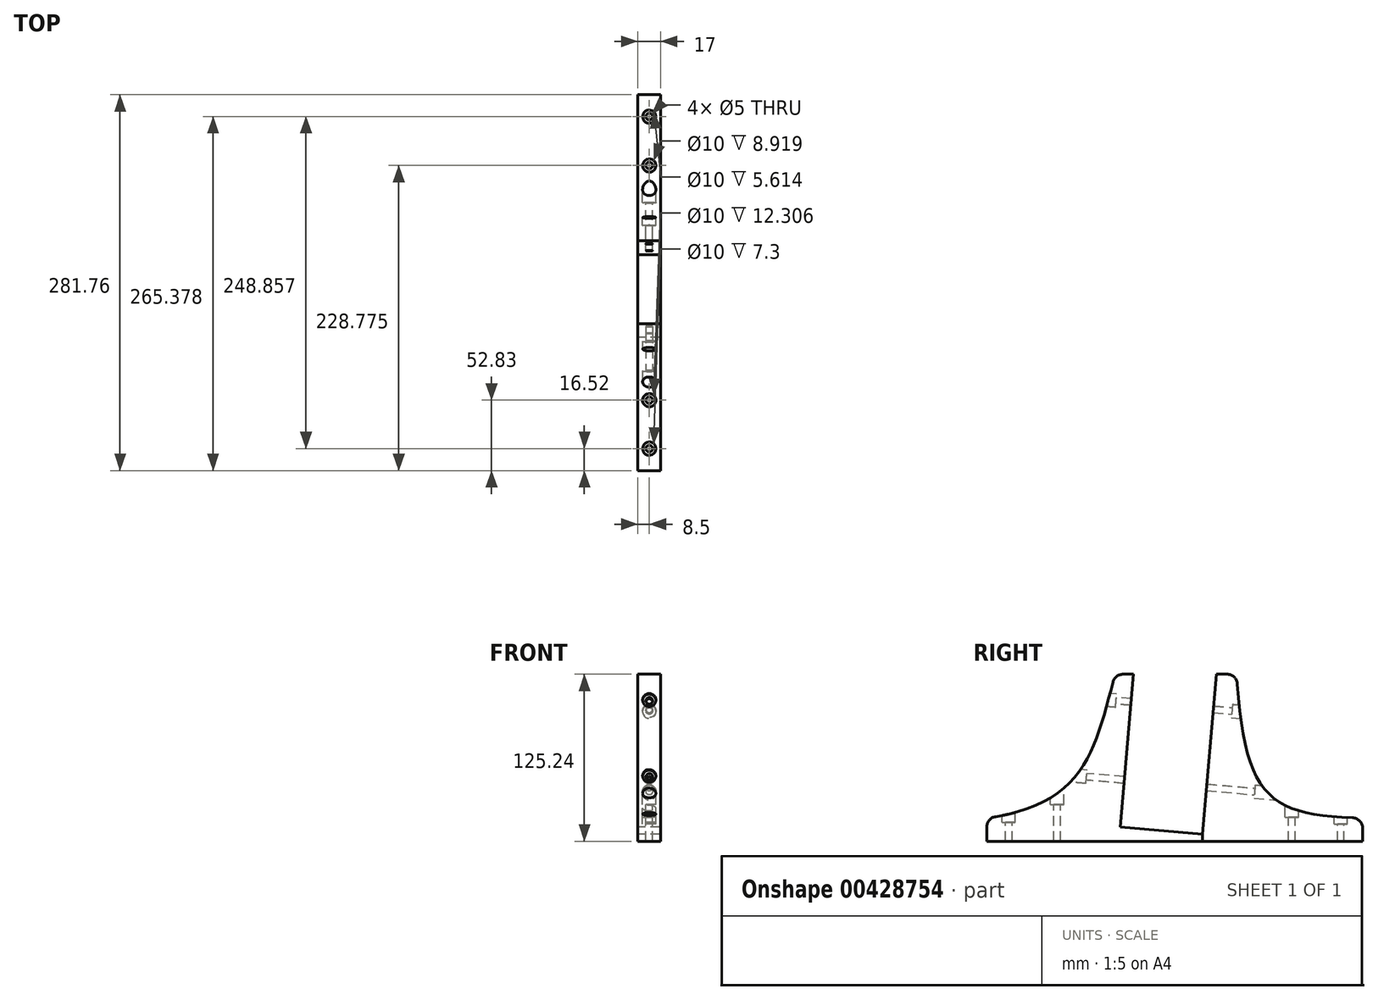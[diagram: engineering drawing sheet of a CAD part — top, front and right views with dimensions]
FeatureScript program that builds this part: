
annotation { "Feature Type Name" : "Feature", "Feature Type Description" : "" }
export const myFeature = defineFeature(function(context is Context, id is Id, definition is map)
    precondition{}
    {
        {
            var Q0;
            Q0=qCreatedBy(makeId("Right.planeOp"),FACE);
            var sketch = newSketch(context, id + "F0", { "sketchPlane" : qUnion([Q0])});
            skLineSegment(sketch, "E0.bottom", {"start": v(0, 0) * mm, "end": v(61.76, -5.4) * mm});
            skLineSegment(sketch, "E0.top", {"start": v(104.59, 1195.43) * mm, "end": v(166.35, 1190.03) * mm});
            skLineSegment(sketch, "E0.left", {"start": v(0, 0) * mm, "end": v(104.59, 1195.43) * mm});
            skLineSegment(sketch, "E0.right", {"start": v(61.76, -5.4) * mm, "end": v(166.35, 1190.03) * mm});
            skLineSegment(sketch, "E1", {"start": v(-100, -5.4) * mm, "end": v(-100, 6.83) * mm});
            skPoint(sketch, "E2.endSnap0", {"position": v(-29.12, -5.4) * mm});
            skLineSegment(sketch, "E3", {"start": v(-3.76, 114.6) * mm, "end": v(10.03, 114.6) * mm});
            skFitSpline(sketch, "E4", {"points": [v(-3.76, 114.6) * mm, v(-100, 6.83) * mm], "startDerivative": vector(-42.9, -159.15) * mm, "endDerivative": vector(-227.38, -28.7) * mm});
            skLineSegment(sketch, "E5", {"start": v(72.26, 114.6) * mm, "end": v(87.42, 114.6) * mm});
            skLineSegment(sketch, "E6", {"start": v(181.76, -5.4) * mm, "end": v(181.76, 6.83) * mm});
            skFitSpline(sketch, "E7", {"points": [v(87.42, 114.6) * mm, v(181.76, 6.83) * mm], "startDerivative": vector(16.8, -278.9) * mm, "endDerivative": vector(212.62, -4.06) * mm});
            skLineSegment(sketch, "E8", {"start": v(-100, -5.4) * mm, "end": v(-100, -10.64) * mm});
            skLineSegment(sketch, "E9", {"start": v(-100, -10.64) * mm, "end": v(181.76, -10.64) * mm});
            skLineSegment(sketch, "E10", {"start": v(181.76, -10.64) * mm, "end": v(181.76, -5.4) * mm});
            skLineSegment(sketch, "E11", {"start": v(61.76, -5.4) * mm, "end": v(61.76, -10.64) * mm});
            skSolve(sketch);
        }
        {
            var Q0;
            {var subQ1=sQuery(id+"F0.wireOp",EDGE,"E0.bottom");Q0=makeQuery(id+"F0.imprint","IMPRINT",FACE,{"disambiguationData":[TD([[makeQuery(id+"F0.imprint","IMPRINT",EDGE,{"derivedFrom":subQ1}),-1.0]])]});}
            extrude(context, id + "F1", {"entities" : qUnion([Q0]), "depth" : 17 * mm});
        }
        {
            var Q0;
            {var subQ0=sQuery(id+"F0.wireOp",EDGE,"E5");Q0=makeQuery(id+"F0.imprint","IMPRINT",FACE,{"disambiguationData":[TD([[makeQuery(id+"F0.imprint","IMPRINT",EDGE,{"derivedFrom":subQ0}),-1.0]])]});}
            extrude(context, id + "F2", {"entities" : qUnion([Q0]), "depth" : 17 * mm});
        }
        {
            var Q0;
            Q0=makeQuery(id+"F1.opExtrude","SWEPT_EDGE",EDGE,{"disambiguationData":[OSD([sQuery(id+"F0.wireOp",EDGE,"E1"),sQuery(id+"F0.wireOp",EDGE,"E4")])]});
            var Q1;
            Q1=makeQuery(id+"F1.opExtrude","SWEPT_EDGE",EDGE,{"disambiguationData":[OSD([sQuery(id+"F0.wireOp",EDGE,"E3"),sQuery(id+"F0.wireOp",EDGE,"E4")])]});
            var Q2;
            Q2=makeQuery(id+"F1.opExtrude","SWEPT_EDGE",EDGE,{"disambiguationData":[OSD([sQuery(id+"F0.wireOp",EDGE,"E6"),sQuery(id+"F0.wireOp",EDGE,"E7")])]});
            var Q3;
            Q3=makeQuery(id+"F1.opExtrude","SWEPT_EDGE",EDGE,{"disambiguationData":[OSD([sQuery(id+"F0.wireOp",EDGE,"E5"),sQuery(id+"F0.wireOp",EDGE,"E7")])]});
            var Q4;
            Q4=makeQuery(id+"F2.opExtrude","SWEPT_EDGE",EDGE,{"disambiguationData":[OSD([sQuery(id+"F0.wireOp",EDGE,"E5"),sQuery(id+"F0.wireOp",EDGE,"E7")])]});
            var Q5;
            Q5=makeQuery(id+"F2.opExtrude","SWEPT_EDGE",EDGE,{"disambiguationData":[OSD([sQuery(id+"F0.wireOp",EDGE,"E6"),sQuery(id+"F0.wireOp",EDGE,"E7")])]});
            fillet(context, id + "F3", {"entities" : qUnion([Q0, Q1, Q2, Q3, Q4, Q5]), "radius" : 8 * mm, "tangentPropagation" : true, "allowEdgeOverflow" : false});
        }
        {
            var Q0;
            Q0=makeQuery(id+"F1.opExtrude","SWEPT_FACE",FACE,{"disambiguationData":[OSD([sQuery(id+"F0.wireOp",EDGE,"E0.left")])]});
            cPlane(context, id + "F4", {"entities" : qUnion([Q0]), "cplaneType" : CPlaneType.OFFSET, "offset" : 53 * mm, "oppositeDirection" : true, "width" : 150 * mm, "height" : 150 * mm});
        }
        {
            var Q0;
            Q0=qCreatedBy(id+"F4.planeOp",FACE);
            var sketch = newSketch(context, id + "F5", { "sketchPlane" : qUnion([Q0])});
            skFitSpline(sketch, "E12.0.0", {"points": [v(-17, -3.65) * mm, v(-17, 12.48) * mm, v(-17, 59.74) * mm, v(-17, 113.83) * mm]});
            skLineSegment(sketch, "E12.0.1", {"start": v(-17, 107.75) * mm, "end": v(0, 107.75) * mm});
            skFitSpline(sketch, "E12.0.2", {"points": [v(0, 113.83) * mm, v(0, 59.74) * mm, v(0, 12.48) * mm, v(0, -3.65) * mm]});
            skLineSegment(sketch, "E12.0.3", {"start": v(0, -0.36) * mm, "end": v(-17, -0.36) * mm});
            skPoint(sketch, "E13", {"position": v(-8.5, 94.03) * mm});
            skPoint(sketch, "E13.positionSnap0", {"position": v(-8.5, 107.75) * mm});
            skPoint(sketch, "E14", {"position": v(-8.5, 35.3) * mm});
            skSolve(sketch);
        }
        {
            var Q0;
            Q0=sQuery(id+"F5.wireOp",VERTEX,"E13");
            var Q1;
            Q1=sQuery(id+"F5.wireOp",VERTEX,"E14");
            var Q2;
            Q2=makeQuery(id+"F1.opExtrude","SWEPT_BODY",BODY,{"disambiguationData":[OSD([sQuery(id+"F0.wireOp",EDGE,"E0.bottom"),sQuery(id+"F0.wireOp",EDGE,"E0.left"),sQuery(id+"F0.wireOp",EDGE,"E1"),sQuery(id+"F0.wireOp",EDGE,"E3"),sQuery(id+"F0.wireOp",EDGE,"E4"),sQuery(id+"F0.wireOp",EDGE,"E8"),sQuery(id+"F0.wireOp",EDGE,"E9"),sQuery(id+"F0.wireOp",EDGE,"E11")])]});
            hole(context, id + "F6", {"style" : HoleStyle.C_BORE, "endStyle" : HoleEndStyle.THROUGH, "oppositeDirection" : true, "holeDiameter" : 5 * mm, "cBoreDiameter" : 10 * mm, "cBoreDepth" : 5 * mm, "tappedDepth" : 12 * mm, "tapClearance" : 3, "locations" : qUnion([Q0, Q1]), "scope" : qUnion([Q2])});
        }
        {
            var Q0;
            Q0=makeQuery(id+"F2.opExtrude","SWEPT_FACE",FACE,{"disambiguationData":[OSD([sQuery(id+"F0.wireOp",EDGE,"E0.right")])]});
            cPlane(context, id + "F7", {"entities" : qUnion([Q0]), "cplaneType" : CPlaneType.OFFSET, "offset" : 68 * mm, "oppositeDirection" : true, "width" : 150 * mm, "height" : 150 * mm});
        }
        {
            var Q0;
            Q0=qCreatedBy(id+"F7.planeOp",FACE);
            var sketch = newSketch(context, id + "F8", { "sketchPlane" : qUnion([Q0])});
            skPoint(sketch, "E15.0", {"position": v(8.5, 94.03) * mm});
            skPoint(sketch, "E16.0", {"position": v(8.5, 35.3) * mm});
            skSolve(sketch);
        }
        {
            var Q0;
            Q0=sQuery(id+"F8.wireOp",VERTEX,"E15.0");
            var Q1;
            Q1=sQuery(id+"F8.wireOp",VERTEX,"E16.0");
            var Q2;
            Q2=makeQuery(id+"F2.opExtrude","SWEPT_BODY",BODY,{"disambiguationData":[OSD([sQuery(id+"F0.wireOp",EDGE,"E0.right"),sQuery(id+"F0.wireOp",EDGE,"E5"),sQuery(id+"F0.wireOp",EDGE,"E6"),sQuery(id+"F0.wireOp",EDGE,"E7"),sQuery(id+"F0.wireOp",EDGE,"E9"),sQuery(id+"F0.wireOp",EDGE,"E10"),sQuery(id+"F0.wireOp",EDGE,"E11")])]});
            hole(context, id + "F9", {"style" : HoleStyle.C_BORE, "endStyle" : HoleEndStyle.THROUGH, "oppositeDirection" : true, "holeDiameter" : 5 * mm, "cBoreDiameter" : 10 * mm, "cBoreDepth" : 5 * mm, "tappedDepth" : 12 * mm, "tapClearance" : 3, "locations" : qUnion([Q0, Q1]), "scope" : qUnion([Q2])});
        }
        {
            var Q0;
            Q0=makeQuery(id+"F1.opExtrude","SWEPT_FACE",FACE,{"disambiguationData":[OSD([sQuery(id+"F0.wireOp",EDGE,"E9")])]});
            cPlane(context, id + "F10", {"entities" : qUnion([Q0]), "cplaneType" : CPlaneType.OFFSET, "offset" : 73.2 * mm, "oppositeDirection" : true, "width" : 150 * mm, "height" : 150 * mm});
        }
        {
            var Q0;
            Q0=qCreatedBy(id+"F10.planeOp",FACE);
            var sketch = newSketch(context, id + "F11", { "sketchPlane" : qUnion([Q0])});
            skLineSegment(sketch, "E17.0.0", {"start": v(0, 100) * mm, "end": v(0, -61.76) * mm});
            skLineSegment(sketch, "E17.0.1", {"start": v(0, -61.76) * mm, "end": v(17, -61.76) * mm});
            skLineSegment(sketch, "E17.0.2", {"start": v(17, -61.76) * mm, "end": v(17, 100) * mm});
            skLineSegment(sketch, "E17.0.3", {"start": v(17, 100) * mm, "end": v(0, 100) * mm});
            skLineSegment(sketch, "E18.0.0", {"start": v(0, -61.76) * mm, "end": v(0, -181.76) * mm});
            skLineSegment(sketch, "E18.0.1", {"start": v(0, -181.76) * mm, "end": v(17, -181.76) * mm});
            skLineSegment(sketch, "E18.0.2", {"start": v(17, -181.76) * mm, "end": v(17, -61.76) * mm});
            skLineSegment(sketch, "E18.0.3", {"start": v(17, -61.76) * mm, "end": v(0, -61.76) * mm});
            skPoint(sketch, "E19", {"position": v(8.5, 83.48) * mm});
            skPoint(sketch, "E19.positionSnap0", {"position": v(8.5, 100) * mm});
            skPoint(sketch, "E20", {"position": v(8.5, 47.17) * mm});
            skPoint(sketch, "E21", {"position": v(8.5, -165.38) * mm});
            skPoint(sketch, "E22", {"position": v(8.5, -128.78) * mm});
            skSolve(sketch);
        }
        {
            var Q0;
            Q0=sQuery(id+"F11.wireOp",VERTEX,"E22");
            var Q1;
            Q1=sQuery(id+"F11.wireOp",VERTEX,"E21");
            var Q2;
            Q2=sQuery(id+"F11.wireOp",VERTEX,"E19");
            var Q3;
            Q3=sQuery(id+"F11.wireOp",VERTEX,"E20");
            var Q4;
            Q4=makeQuery(id+"F1.opExtrude","SWEPT_BODY",BODY,{"disambiguationData":[OSD([sQuery(id+"F0.wireOp",EDGE,"E0.bottom"),sQuery(id+"F0.wireOp",EDGE,"E0.left"),sQuery(id+"F0.wireOp",EDGE,"E1"),sQuery(id+"F0.wireOp",EDGE,"E3"),sQuery(id+"F0.wireOp",EDGE,"E4"),sQuery(id+"F0.wireOp",EDGE,"E8"),sQuery(id+"F0.wireOp",EDGE,"E9"),sQuery(id+"F0.wireOp",EDGE,"E11")])]});
            var Q5;
            Q5=makeQuery(id+"F2.opExtrude","SWEPT_BODY",BODY,{"disambiguationData":[OSD([sQuery(id+"F0.wireOp",EDGE,"E0.right"),sQuery(id+"F0.wireOp",EDGE,"E5"),sQuery(id+"F0.wireOp",EDGE,"E6"),sQuery(id+"F0.wireOp",EDGE,"E7"),sQuery(id+"F0.wireOp",EDGE,"E9"),sQuery(id+"F0.wireOp",EDGE,"E10"),sQuery(id+"F0.wireOp",EDGE,"E11")])]});
            hole(context, id + "F12", {"style" : HoleStyle.C_BORE, "endStyle" : HoleEndStyle.THROUGH, "oppositeDirection" : true, "holeDiameter" : 5 * mm, "cBoreDiameter" : 10 * mm, "cBoreDepth" : 5 * mm, "tappedDepth" : 12 * mm, "tapClearance" : 3, "locations" : qUnion([Q0, Q1, Q2, Q3]), "scope" : qUnion([Q4, Q5])});
        }
    });
